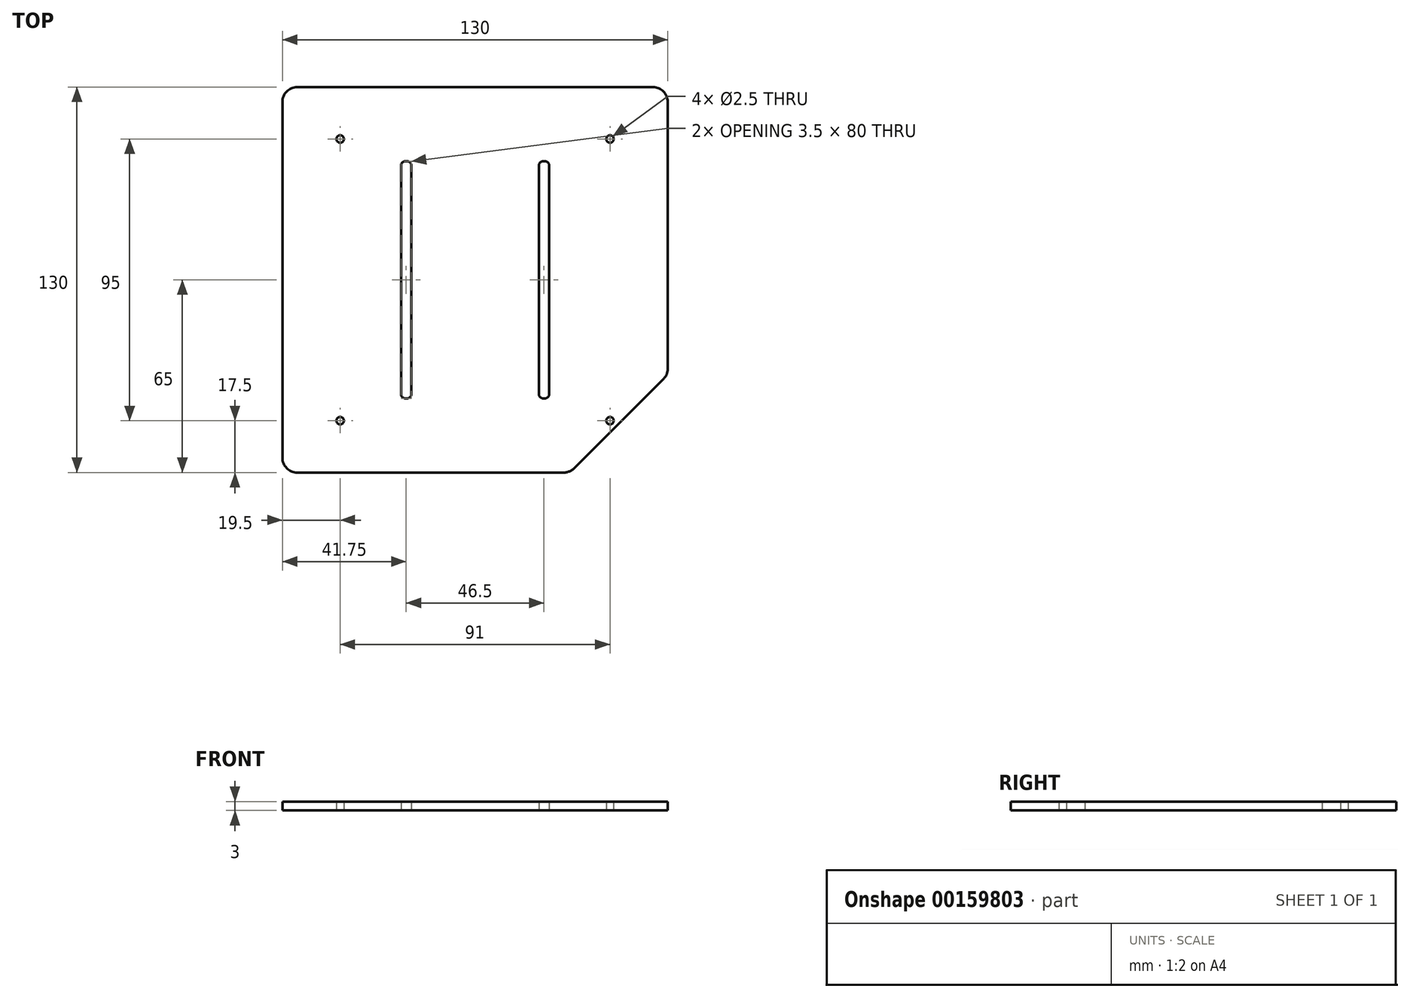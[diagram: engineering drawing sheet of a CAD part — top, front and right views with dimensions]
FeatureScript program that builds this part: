
annotation { "Feature Type Name" : "Feature", "Feature Type Description" : "" }
export const myFeature = defineFeature(function(context is Context, id is Id, definition is map)
    precondition{}
    {
        {
            var Q0;
            Q0=qCreatedBy(makeId("Top.planeOp"),FACE);
            var sketch = newSketch(context, id + "F0", { "sketchPlane" : qUnion([Q0])});
            skLineSegment(sketch, "E0.bottom", {"start": v(29.93, -65) * mm, "end": v(-60, -65) * mm});
            skLineSegment(sketch, "E0.top", {"start": v(60, 65) * mm, "end": v(-60, 65) * mm});
            skLineSegment(sketch, "E0.left", {"start": v(65, -29.93) * mm, "end": v(65, 60) * mm});
            skLineSegment(sketch, "E0.right", {"start": v(-65, -60) * mm, "end": v(-65, 60) * mm});
            skPoint(sketch, "E0.middle", {"position": v(0, 0) * mm});
            skCircle(sketch, "E1", {"center": v(-45.5, -47.5) * mm, "radius": 1.25 * mm});
            skCircle(sketch, "E2", {"center": v(45.5, -47.5) * mm, "radius": 1.25 * mm});
            skCircle(sketch, "E3", {"center": v(45.5, 47.5) * mm, "radius": 1.25 * mm});
            skCircle(sketch, "E4", {"center": v(-45.5, 47.5) * mm, "radius": 1.25 * mm});
            skLineSegment(sketch, "E5.bottom", {"start": v(-23, -40) * mm, "end": v(-23.5, -40) * mm});
            skLineSegment(sketch, "E5.top", {"start": v(-23, 40) * mm, "end": v(-23.5, 40) * mm});
            skLineSegment(sketch, "E5.left", {"start": v(-21.5, -38.5) * mm, "end": v(-21.5, 38.5) * mm});
            skLineSegment(sketch, "E5.right", {"start": v(-25, -38.5) * mm, "end": v(-25, 38.5) * mm});
            skPoint(sketch, "E5.middle", {"position": v(-23.25, 0) * mm});
            skLineSegment(sketch, "E6.bottom", {"start": v(23.5, -40) * mm, "end": v(23, -40) * mm});
            skLineSegment(sketch, "E6.top", {"start": v(23.5, 40) * mm, "end": v(23, 40) * mm});
            skLineSegment(sketch, "E6.left", {"start": v(25, -38.5) * mm, "end": v(25, 38.5) * mm});
            skLineSegment(sketch, "E6.right", {"start": v(21.5, -38.5) * mm, "end": v(21.5, 38.5) * mm});
            skPoint(sketch, "E6.middle", {"position": v(23.25, 0) * mm});
            skPoint(sketch, "E7.visualSharp", {"position": v(-65, 65) * mm});
            skArc(sketch, "E7.filletArc", {"start": v(-60, 65) * mm, "mid": v(-63.54, 63.54) * mm, "end": v(-65, 60) * mm});
            skPoint(sketch, "E8.visualSharp", {"position": v(65, 65) * mm});
            skArc(sketch, "E8.filletArc", {"start": v(65, 60) * mm, "mid": v(63.54, 63.54) * mm, "end": v(60, 65) * mm});
            skPoint(sketch, "E9.visualSharp", {"position": v(65, -65) * mm});
            skPoint(sketch, "E10.visualSharp", {"position": v(-65, -65) * mm});
            skArc(sketch, "E10.filletArc", {"start": v(-65, -60) * mm, "mid": v(-63.54, -63.54) * mm, "end": v(-60, -65) * mm});
            skPoint(sketch, "E11.visualSharp", {"position": v(-25, -40) * mm});
            skArc(sketch, "E11.filletArc", {"start": v(-25, -38.5) * mm, "mid": v(-24.56, -39.56) * mm, "end": v(-23.5, -40) * mm});
            skPoint(sketch, "E12.visualSharp", {"position": v(-21.5, -40) * mm});
            skArc(sketch, "E12.filletArc", {"start": v(-23, -40) * mm, "mid": v(-21.94, -39.56) * mm, "end": v(-21.5, -38.5) * mm});
            skPoint(sketch, "E13.visualSharp", {"position": v(-25, 40) * mm});
            skArc(sketch, "E13.filletArc", {"start": v(-23.5, 40) * mm, "mid": v(-24.56, 39.56) * mm, "end": v(-25, 38.5) * mm});
            skPoint(sketch, "E14.visualSharp", {"position": v(-21.5, 40) * mm});
            skArc(sketch, "E14.filletArc", {"start": v(-21.5, 38.5) * mm, "mid": v(-21.94, 39.56) * mm, "end": v(-23, 40) * mm});
            skPoint(sketch, "E15.visualSharp", {"position": v(21.5, 40) * mm});
            skArc(sketch, "E15.filletArc", {"start": v(23, 40) * mm, "mid": v(21.94, 39.56) * mm, "end": v(21.5, 38.5) * mm});
            skPoint(sketch, "E16.visualSharp", {"position": v(25, 40) * mm});
            skArc(sketch, "E16.filletArc", {"start": v(25, 38.5) * mm, "mid": v(24.56, 39.56) * mm, "end": v(23.5, 40) * mm});
            skPoint(sketch, "E17.visualSharp", {"position": v(21.5, -40) * mm});
            skArc(sketch, "E17.filletArc", {"start": v(21.5, -38.5) * mm, "mid": v(21.94, -39.56) * mm, "end": v(23, -40) * mm});
            skPoint(sketch, "E18.visualSharp", {"position": v(25, -40) * mm});
            skArc(sketch, "E18.filletArc", {"start": v(23.5, -40) * mm, "mid": v(24.56, -39.56) * mm, "end": v(25, -38.5) * mm});
            skLineSegment(sketch, "E19", {"start": v(33.46, -63.54) * mm, "end": v(63.54, -33.46) * mm});
            skPoint(sketch, "E20.newPointB", {"position": v(32, -65) * mm});
            skArc(sketch, "E20.filletArc", {"start": v(29.93, -65) * mm, "mid": v(31.84, -64.62) * mm, "end": v(33.46, -63.54) * mm});
            skPoint(sketch, "E21.newPointB", {"position": v(65, -32) * mm});
            skArc(sketch, "E21.filletArc", {"start": v(63.54, -33.46) * mm, "mid": v(64.62, -31.84) * mm, "end": v(65, -29.93) * mm});
            skSolve(sketch);
        }
        {
            var Q0;
            Q0=makeQuery(id+"F0.imprint","IMPRINT",FACE,{"disambiguationData":[TD([[makeQuery(id+"F0.imprint","IMPRINT",EDGE,{"derivedFrom":sQuery(id+"F0.wireOp",EDGE,"E0.bottom")}),-1.0]])]});
            extrude(context, id + "F1", {"entities" : qUnion([Q0]), "depth" : 3 * mm});
        }
    });
